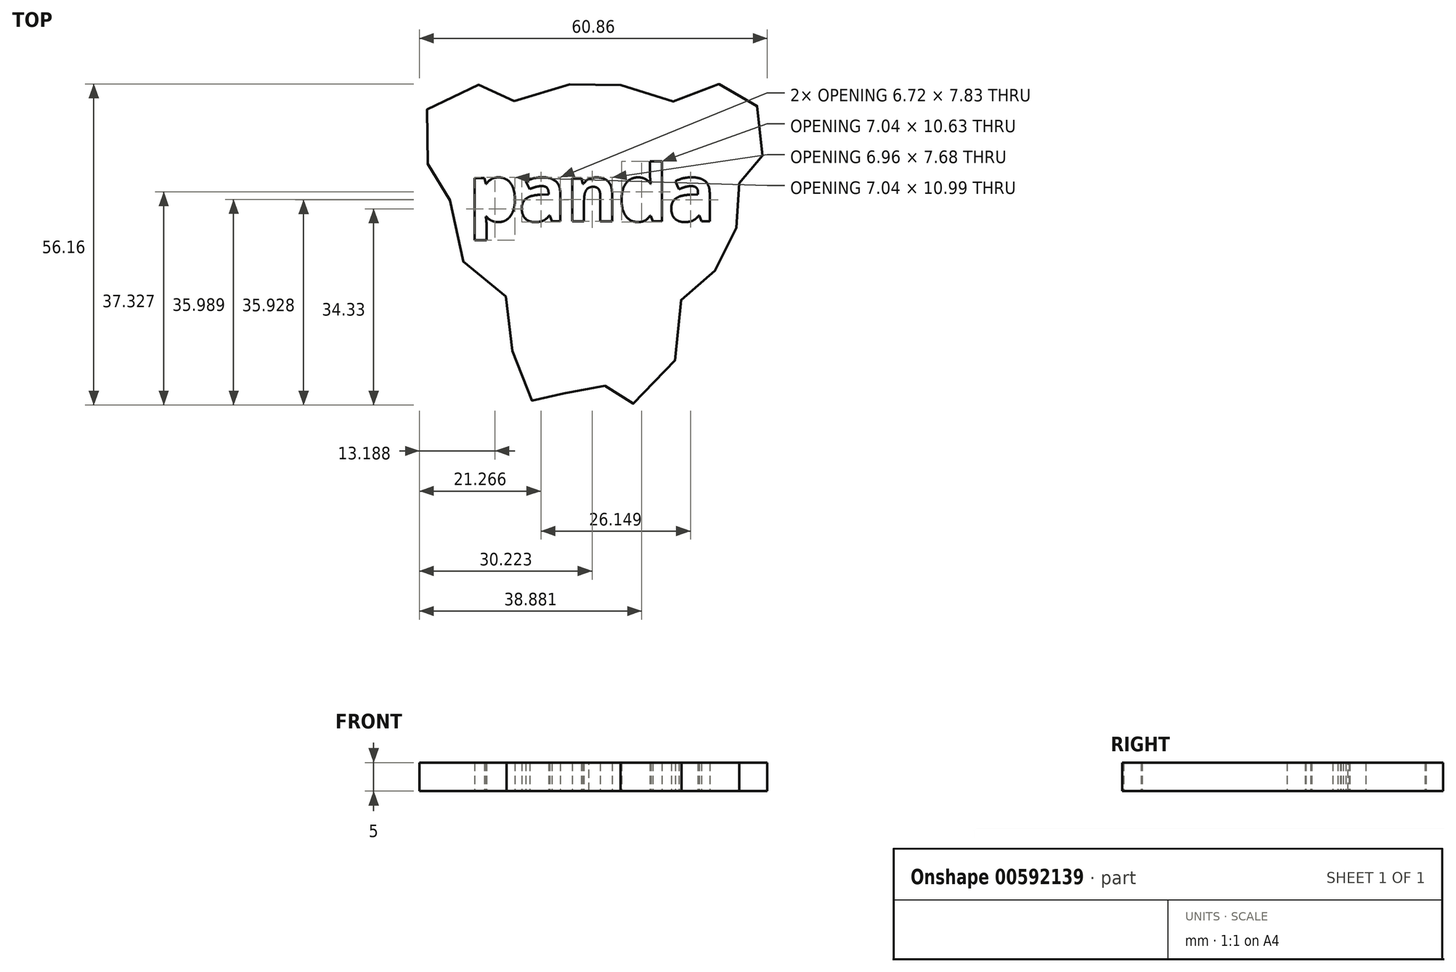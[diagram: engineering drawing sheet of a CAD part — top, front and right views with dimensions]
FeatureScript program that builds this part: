
annotation { "Feature Type Name" : "Feature", "Feature Type Description" : "" }
export const myFeature = defineFeature(function(context is Context, id is Id, definition is map)
    precondition{}
    {
        {
            var Q0;
            Q0=qCreatedBy(makeId("Top.planeOp"),FACE);
            var sketch = newSketch(context, id + "F0", { "sketchPlane" : qUnion([Q0])});
            skPoint(sketch, "E0.28.internal.orphan", {"position": v(6.14, 0) * mm});
            skPoint(sketch, "E0.38.internal.orphan", {"position": v(0, 32.49) * mm});
            skPoint(sketch, "E0.4.internal.orphan", {"position": v(-33.36, 0) * mm});
            skPoint(sketch, "E1.28.internal.snap0", {"position": v(-37.17, 35.07) * mm});
            skFitSpline(sketch, "E1", {"points": [v(-51.06, 32.11) * mm, v(-44.84, 34.46) * mm, v(-39.99, 35.07) * mm, v(-35.2, 35.07) * mm, v(-29.82, 34.39) * mm, v(-23.53, 31.96) * mm, v(-23.15, 32.11) * mm, v(-19.5, 34.16) * mm, v(-14.88, 35.07) * mm, v(-12.15, 33.93) * mm, v(-8.89, 31.58) * mm, v(-6.8, 27.64) * mm, v(-7.6, 22.55) * mm, v(-8.8, 20.66) * mm, v(-11.39, 18.23) * mm, v(-11.7, 17.78) * mm, v(-11.7, 14.67) * mm, v(-12.07, 10.65) * mm, v(-12.9, 7.23) * mm, v(-14.95, 3.67) * mm, v(-19.28, -0.58) * mm, v(-21.55, -1.95) * mm, v(-21.86, -3.39) * mm, v(-21.86, -7.64) * mm, v(-25.95, -19.85) * mm, v(-30.2, -20.78) * mm, v(-32.4, -19.01) * mm, v(-32.55, -17.95) * mm, v(-37.17, -17.72) * mm, v(-41.65, -17.72) * mm, v(-42.34, -18.7) * mm, v(-42.64, -20.15) * mm, v(-45.6, -20.78) * mm, v(-48.25, -20) * mm, v(-49.7, -16.74) * mm, v(-51.97, -8.85) * mm, v(-52.35, -2.48) * mm, v(-52.43, -2.1) * mm, v(-56.45, 0) * mm, v(-60.31, 4.73) * mm, v(-62.06, 9.5) * mm, v(-62.51, 18.16) * mm, v(-62.97, 18.46) * mm, v(-66.3, 21.34) * mm, v(-67.53, 27.4) * mm, v(-65.32, 31.88) * mm, v(-59.56, 35.07) * mm, v(-54.1, 34) * mm, v(-52.5, 33.1) * mm, v(-51.06, 32.11) * mm]});
            skText(sketch, "E2", { "text": "panda", "fontName": "OpenSans-Bold.ttf"});
            const initialGuessF0  = {"E2": [-0.05903, 0.0111, 1, 0, 0.00994]};
            skSetInitialGuess(sketch, initialGuessF0);
            skSolve(sketch);
        }
        {
            var Q0;
            Q0 = qSketchRegion(id + "F0", true);
            extrude(context, id + "F1", {"entities" : qUnion([Q0]), "depth" : 5 * mm, "offsetDistance" : 25 * mm});
        }
    });
